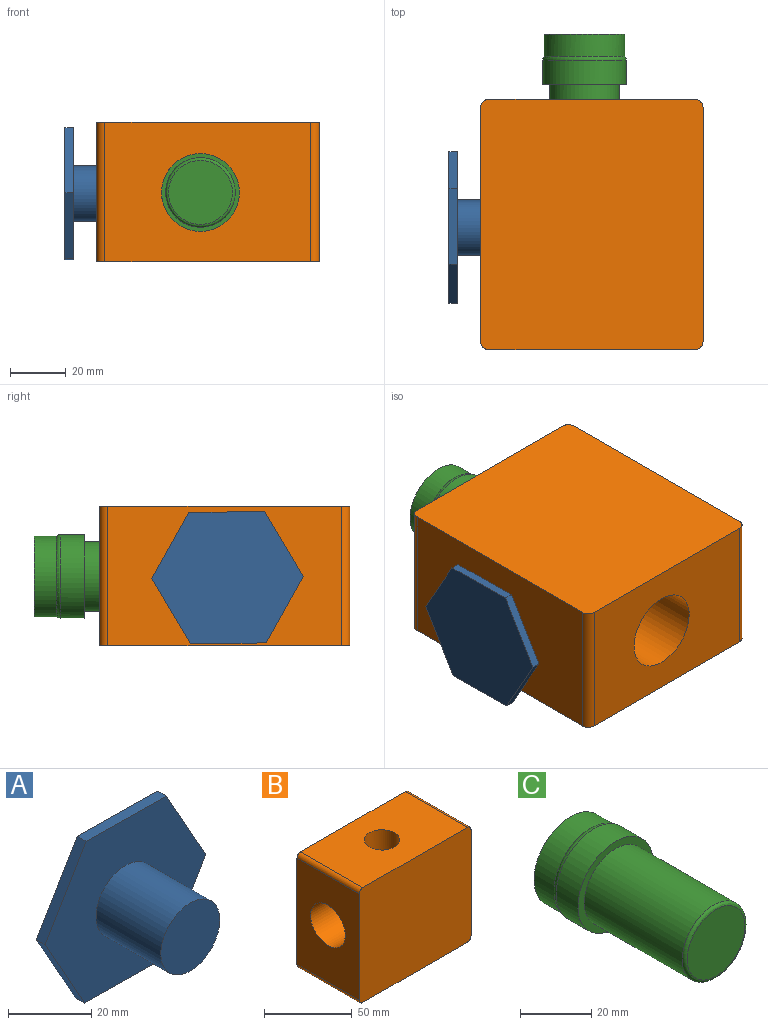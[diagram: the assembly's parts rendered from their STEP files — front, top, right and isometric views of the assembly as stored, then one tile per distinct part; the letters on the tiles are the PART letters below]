
ASSEMBLY  parts=3 mates=2
PART A: 10 faces, bbox 54.5x25x47.6 mm
  f0: cylinder r=10mm len=22mm, axis (0,1,0), area 1382.3mm2, adj f1,f8
  f1: plane 20x20mm, normal (0,-1,0), area 314.2mm2, adj f0
  f2: plane 23.79x13.33mm, normal (-0.87,0,-0.49), area 81.8mm2, adj f3,f7,f8,f9
  f3: plane 27.27x3mm, normal (-0.01,0,-1), area 81.8mm2, adj f2,f4,f8,f9
  f4: plane 23.44x13.94mm, normal (0.86,0,-0.51), area 81.8mm2, adj f3,f5,f8,f9
  f5: plane 23.79x13.33mm, normal (0.87,0,0.49), area 81.8mm2, adj f4,f6,f8,f9
  f6: plane 27.27x3mm, normal (0.01,0,1), area 81.8mm2, adj f5,f7,f8,f9
  f7: plane 23.44x13.94mm, normal (-0.86,0,0.51), area 81.8mm2, adj f2,f6,f8,f9
  f8: plane 54.54x47.58mm, normal (0,-1,0), area 1618mm2, adj f0,f2,f3,f4,f5,f6,f7
  f9: plane 54.54x47.58mm, normal (0,1,0), area 1932.1mm2, adj f2,f3,f4,f5,f6,f7
PART B: 12 faces, bbox 90x50x80 mm
  f0: plane 74x50mm, normal (-1,0,0), area 3084.2mm2, adj f4,f5,f7,f8,f11
  f1: plane 84x50mm, normal (0,0,-1), area 4200mm2, adj f4,f5,f8,f9
  f2: plane 74x50mm, normal (1,0,0), area 3084.2mm2, adj f4,f5,f7,f9,f10
  f3: plane 84x50mm, normal (0,0,1), area 3885.8mm2, adj f4,f5,f6,f10,f11
  f4: plane 90x80mm, normal (0,-1,0), area 7192.3mm2, adj f0,f1,f2,f3,f8,f9,f10,f11
  f5: plane 90x80mm, normal (0,1,0), area 7192.3mm2, adj f0,f1,f2,f3,f8,f9,f10,f11
  f6: cylinder r=10mm len=28.03mm, axis (0,0,1), area 1594.9mm2, adj f3,f7
  f7: cylinder r=14mm len=90mm, axis (-1,0,0), area 7577.1mm2, adj f0,f2,f6
  f8: cylinder r=3mm len=50mm, axis (0,1,0), area 235.6mm2, adj f0,f1,f4,f5
  f9: cylinder r=3mm len=50mm, axis (0,-1,0), area 235.6mm2, adj f1,f2,f4,f5
  f10: cylinder r=3mm len=50mm, axis (0,1,0), area 235.6mm2, adj f2,f3,f4,f5
  f11: cylinder r=3mm len=50mm, axis (0,-1,0), area 235.6mm2, adj f0,f3,f4,f5
PART C: 8 faces, bbox 32.5x58x32.5 mm
  f0: cylinder r=15mm len=30mm, axis (0,1,0), area 817.8mm2, adj f1,f7
  f1: plane 30x30mm, normal (0,-1,0), area 216mm2, adj f0,f2
  f2: cylinder r=12.5mm len=39mm, axis (0,1,0), area 3063.1mm2, adj f1,f4
  f3: plane 23x23mm, normal (0,-1,0), area 415.5mm2, adj f4
  f4: torus R=11.5mm, axis (0,-1,0), area 119.8mm2, adj f2,f3
  f5: cylinder r=14.5mm len=29mm, axis (0,-1,0), area 728.8mm2, adj f6,f7
  f6: plane 29x29mm, normal (0,1,0), area 660.5mm2, adj f5
  f7: torus R=13mm, axis (0,1,0), area 134.7mm2, adj f0,f5
PLACE A rot(axis=(0,0,1),90deg) t=(-9.2,-2.21,-36.81)mm
PLACE B rot(axis=(-0.58,-0.58,0.58),120deg) t=(52.49,-21.97,-48.74)mm
PLACE C t=(92.78,48.52,-30.14)mm
MATE cylindrical B.f7 <-> C.f0  axis (0,-1,0) through (39.52,33.07,-23.91)mm
MATE cylindrical A.f0 <-> B.f6  axis (-1,0,0) through (4.8,-12.97,-24.34)mm
